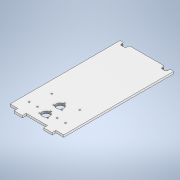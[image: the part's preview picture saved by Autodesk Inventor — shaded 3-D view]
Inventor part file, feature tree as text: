
AUTODESK INVENTOR PART (.ipt)
format: ipt  version: 2020 (Build 240168000, 168)  size: 218,112 bytes
history: native  units: mm
features: extrude x4, sketch x4, pattern_linear x3
ambient origin geometry x8: Origin, YZ Plane, XZ Plane, XY Plane, X Axis, Y Axis, Z Axis, Center Point
bodies: Solid1 (feature_tree)
feature tree (11):
  extrude  "base"  Depth=3.0mm
  extrude  "Poke Hole"  Depth=3.0mm
  pattern_linear  "Rectangular Pattern1"  Spacing1=9.0mm  [1 undecoded]
  extrude  "Mount Holes"  Depth=19.7mm
  pattern_linear  "Rectangular Pattern2"  Spacing1=1.5mm  [1 undecoded]
  extrude  "PCB mount holes"  Depth=126.0mm
  pattern_linear  "Rectangular Pattern3"  Spacing1=18.25mm  [1 undecoded]
  sketch  "Sketch1"  dims[d3=12.7mm d5=3.0mm]
  sketch  "Sketch2"  dims[d7=12.7mm d9=3.0mm]
  sketch  "Sketch3"  dims[d10=9.0mm]
  sketch  "Sketch4"  dims[d11=19.7mm d13=9.0mm d14=19.7mm d16=1.5mm d17=126.0mm d20=18.25mm d21=18.25mm d22=57.15mm d23=9.0mm d24=9.0mm d27=250.0mm d28=250.0mm d29=5.0mm d30=0.0mm d31=18.0mm d32=21.5mm d33=5.0mm d34=0.0mm d35=20.0mm d37=33.0mm d38=10.0mm d40=33.0mm d41=3.0mm d42=11.1mm d43=30.0mm d45=360.0deg d47=5.0mm d48=0.0mm d49=20.0mm d51=33.0mm d52=33.0mm d53=83.0mm d54=3.7mm d55=3.3mm d56=3.3mm d57=19.75mm d58=3.3mm d59=44.5mm d62=10.0mm d63=0.0mm d64=20.0mm d66=66.0mm]
note: 3 required parameter values undecoded (feature->parameter linkage not recoverable at this tier; creation-order binding heuristic only, values carry confidence <= 0.55)
